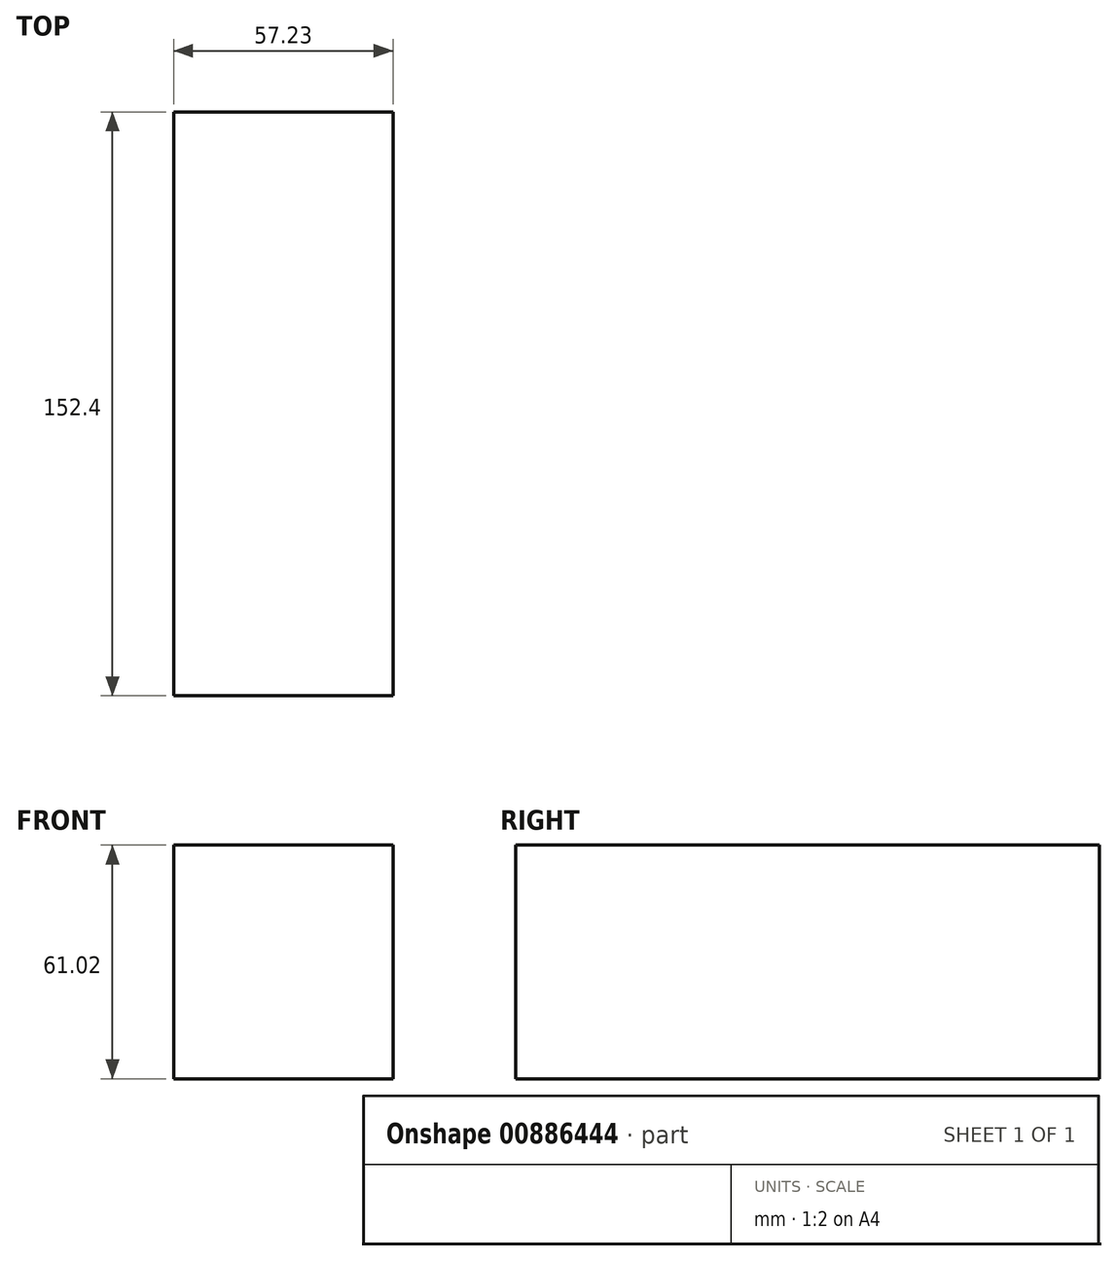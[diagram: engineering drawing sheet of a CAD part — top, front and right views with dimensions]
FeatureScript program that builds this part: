
annotation { "Feature Type Name" : "Feature", "Feature Type Description" : "" }
export const myFeature = defineFeature(function(context is Context, id is Id, definition is map)
    precondition{}
    {
        {
            var Q0;
            Q0=qCreatedBy(makeId("Front.planeOp"),FACE);
            var sketch = newSketch(context, id + "F0", { "sketchPlane" : qUnion([Q0])});
            skLineSegment(sketch, "E0.bottom", {"start": v(-15.79, 30.51) * mm, "end": v(-73.02, 30.51) * mm});
            skLineSegment(sketch, "E0.top", {"start": v(-15.79, -30.51) * mm, "end": v(-73.02, -30.51) * mm});
            skLineSegment(sketch, "E0.left", {"start": v(-15.79, 30.51) * mm, "end": v(-15.79, -30.51) * mm});
            skLineSegment(sketch, "E0.right", {"start": v(-73.02, 30.51) * mm, "end": v(-73.02, -30.51) * mm});
            skPoint(sketch, "E0.middle", {"position": v(-44.4, 0) * mm});
            skSolve(sketch);
        }
        {
            var Q0;
            Q0 = qSketchRegion(id + "F0", true);
            extrude(context, id + "F1", {"entities" : qUnion([Q0]), "oppositeDirection" : true, "depth" : 152.4 * mm, "offsetDistance" : 25.4 * mm});
        }
    });
